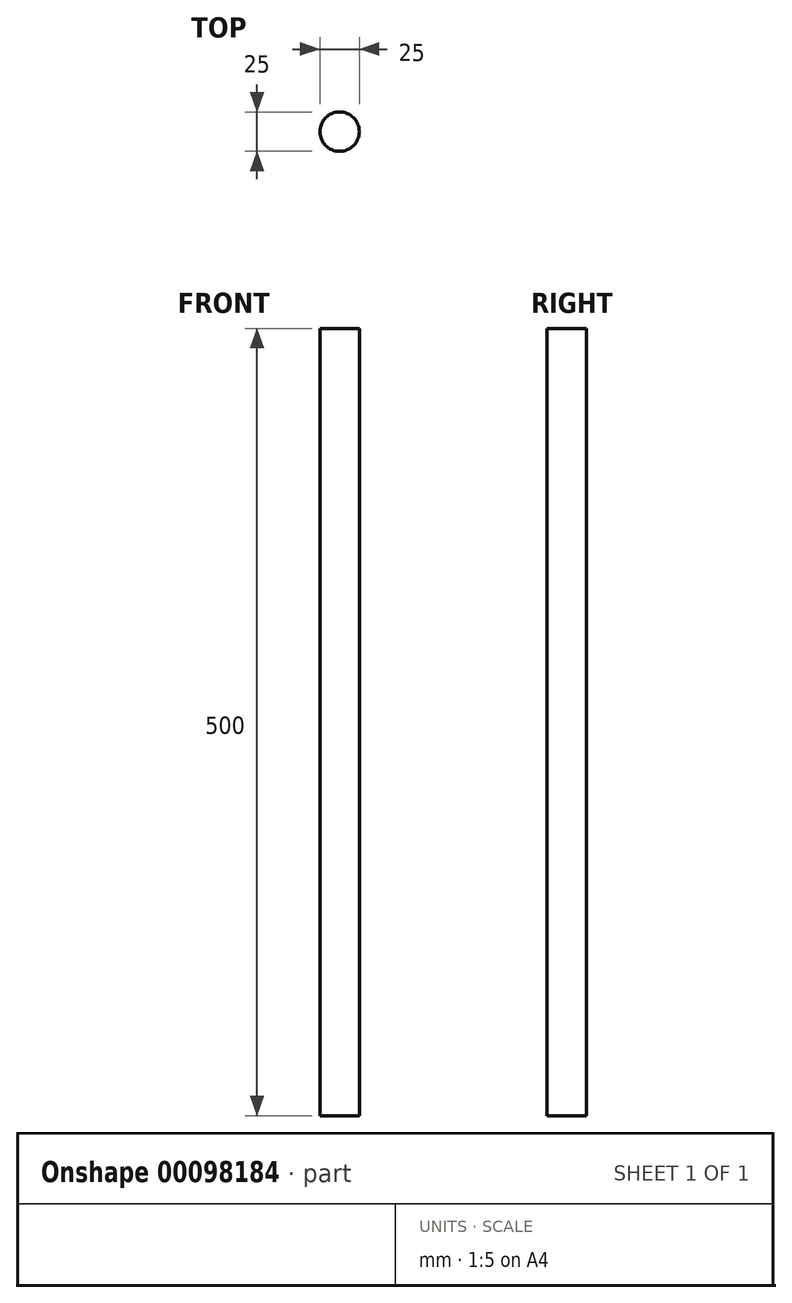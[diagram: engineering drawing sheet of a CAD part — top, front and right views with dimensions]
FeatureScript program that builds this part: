
annotation { "Feature Type Name" : "Feature", "Feature Type Description" : "" }
export const myFeature = defineFeature(function(context is Context, id is Id, definition is map)
    precondition{}
    {
        {
            var Q0;
            Q0=qCreatedBy(makeId("Top.planeOp"),FACE);
            var sketch = newSketch(context, id + "F0", { "sketchPlane" : qUnion([Q0])});
            skCircle(sketch, "E0", {"center": v(0, 0) * mm, "radius": 12.5 * mm});
            skSolve(sketch);
        }
        {
            var Q0;
            Q0=makeQuery(id+"F0.imprint","IMPRINT",FACE,{"disambiguationData":[TD([[makeQuery(id+"F0.imprint","IMPRINT",EDGE,{"derivedFrom":sQuery(id+"F0.wireOp",EDGE,"E0")}),1.0]])]});
            extrude(context, id + "F1", {"entities" : qUnion([Q0]), "depth" : 500 * mm});
        }
    });
